# Revit family: PRD_AR_MltFnctnDspnsrs_STRATOSPaperTowelWasteBinCombination_STRX602E
name_source: partatom
category: Specialty Equipment
revit_build: Autodesk Revit 2018 (Build: 20190510_1515(x64)
units: mm (PartAtom-declared; Revit-internal decimal feet)

## family parameters
Cut with Voids When Loaded = Yes
Host = Face
OmniClass Number = 23.40.20.21.17
OmniClass Title = Paper Towel Dispensers, Disposal Units
Part Type = Normal
Room Calculation Point = No
Round Connector Dimension = Use Diameter
Shared = No

## types (1)
- STRX602E
    AssetType = Fixed
    BIMObjectName = PRD_AR_MultiFunctionDispensers_STRATOSPaperTowelWasteBinCombination_STRX602E
    Category = Pr_40_70_22_52, Multi-function dispensers
    CombinationPart1 = Paper towel dispenser
    CombinationPart2 = Waste bin
    Default Elevation = 850 mm  [stored 2.78871 ft]
    Description = Paper towel dispenser, waste bin combination for recessed mounting, stainless steel, surface satin finished, front with InoxPlus surface refinement for the reduction of finger marks and better cleaning characteristics (easy to clean), material thickness 1.5 mm, curved front cover, cylinder lock with KWC standard key, inspection windows on front, loading capacity 300 - 400 pcs. of paper depending on convolution, waste bin with approx. 22 liter capacity, integrated bag holder, includes stainless steel screws and dowels.
    DispenserMaterial = PRD_AR_StainlessSteel_SatinFinished
    DurationUnit = year
    Features = stainless steel, surface satin finished
    FillingQuantity1 = 400
    FillingQuantity1Uom = Pieces
    FillingQuantity2 = 22
    FillingQuantity2Uom = Liter
    Finish = satin finished
    GrossWeight = 18.22 kg
    IfcExportAs = IfcFurnitureType
    IfcExportType = USERDEFINED
    IntegralAccessories = incl. stainless steel screws and dowels
    IsBuiltIn = TRUE
    Lock1 = Key-lock
    Lock2 = Key-lock
    MainColor = stainless steel
    Manufacturer = KWC Group AG
    ManufacturerName = KWC Group AG
    ManufacturerURL = www.kwc.com
    Material = stainless steel
    MaterialCode = 1.4301
    MaterialThickness = 1.50 mm
    Model = STRX602E
    ModelNumber = 2000057227
    ModelReference = STRX602E
    NBSDescription = Multi-function dispensers
    NBSReference = 45-35-72/384
    Name = Paper Towel Waste Bin Combination STRX602E
    NetWeight = 15.65 kg
    NominalDepth = 203 mm  [stored 0.66601 ft]
    NominalHeight = 1162 mm  [stored 3.81234 ft]
    NominalWidth = 328 mm  [stored 1.07612 ft]
    Offset = 0 mm  [stored 0 ft]
    ProductInformation = https://pim.kwc.com
    Size = 328 x 1162 x 203 mm
    SurfaceTreatment = InoxPlus (anti fingerprint)
    TypeOfConsumable1 = Paper towel
    TypeOfFixing = Screw
    TypeOfMounting = Recessed mounting
    URL = www.kwc.com
    Uniclass2015Code = Pr_40_70_22_52
    Uniclass2015Title = Multi-function dispensers
    Uniclass2015Version = Products v1.10
    Version = 1
    WarrantyDurationUnit = year

note: [stored X ft] marks values corroborated as IEEE doubles in the binary element streams (Revit-internal decimal feet)

## geometry (parser evidence)
native form markers: Sweep x4
no freeform markers — native parametric forms only
